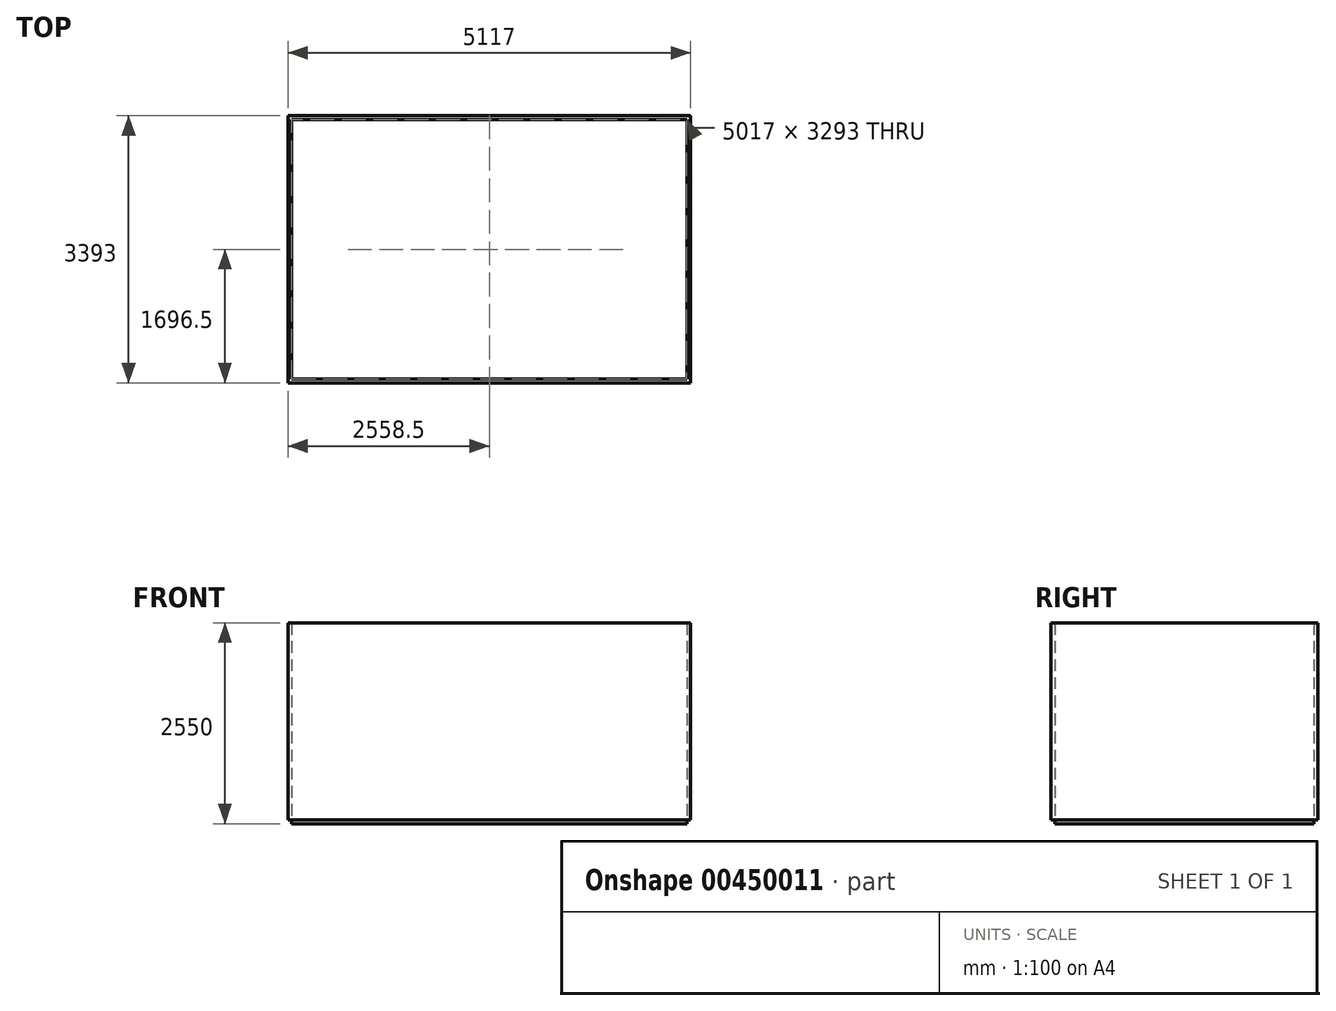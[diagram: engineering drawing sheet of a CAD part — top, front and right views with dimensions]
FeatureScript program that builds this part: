
annotation { "Feature Type Name" : "Feature", "Feature Type Description" : "" }
export const myFeature = defineFeature(function(context is Context, id is Id, definition is map)
    precondition{}
    {
        {
            var Q0;
            Q0=qCreatedBy(makeId("Top.planeOp"),FACE);
            var sketch = newSketch(context, id + "F0", { "sketchPlane" : qUnion([Q0])});
            skLineSegment(sketch, "E0.bottom", {"start": v(0, 0) * mm, "end": v(-5017, 0) * mm});
            skLineSegment(sketch, "E0.top", {"start": v(0, 3293) * mm, "end": v(-5017, 3293) * mm});
            skLineSegment(sketch, "E0.left", {"start": v(0, 0) * mm, "end": v(0, 3293) * mm});
            skLineSegment(sketch, "E0.right", {"start": v(-5017, 0) * mm, "end": v(-5017, 3293) * mm});
            skSolve(sketch);
        }
        {
            var Q0;
            Q0 = qSketchRegion(id + "F0", true);
            extrude(context, id + "F1", {"entities" : qUnion([Q0]), "oppositeDirection" : true, "depth" : 50 * mm});
        }
        {
            var Q0;
            Q0=makeQuery(id+"F1.opExtrude","CAP_FACE",FACE,{"disambiguationData":[OSD([sQuery(id+"F0.wireOp",EDGE,"E0.bottom"),sQuery(id+"F0.wireOp",EDGE,"E0.top"),sQuery(id+"F0.wireOp",EDGE,"E0.left"),sQuery(id+"F0.wireOp",EDGE,"E0.right")])],"isStart":true});
            var sketch = newSketch(context, id + "F2", { "sketchPlane" : qUnion([Q0])});
            skLineSegment(sketch, "E1.0.0", {"start": v(0, 0) * mm, "end": v(0, 3293) * mm});
            skLineSegment(sketch, "E1.0.1", {"start": v(0, 3293) * mm, "end": v(-5017, 3293) * mm});
            skLineSegment(sketch, "E1.0.2", {"start": v(-5017, 3293) * mm, "end": v(-5017, 0) * mm});
            skLineSegment(sketch, "E1.0.3", {"start": v(-5017, 0) * mm, "end": v(0, 0) * mm});
            skLineSegment(sketch, "E2.0", {"start": v(50, -50) * mm, "end": v(50, 3343) * mm});
            skLineSegment(sketch, "E2.1", {"start": v(-5067, -50) * mm, "end": v(50, -50) * mm});
            skLineSegment(sketch, "E2.2", {"start": v(-5067, 3343) * mm, "end": v(-5067, -50) * mm});
            skLineSegment(sketch, "E2.3", {"start": v(50, 3343) * mm, "end": v(-5067, 3343) * mm});
            skSolve(sketch);
        }
        {
            var Q0;
            Q0 = qSketchRegion(id + "F2", true);
            extrude(context, id + "F3", {"entities" : qUnion([Q0]), "depth" : 2500 * mm});
        }
    });
